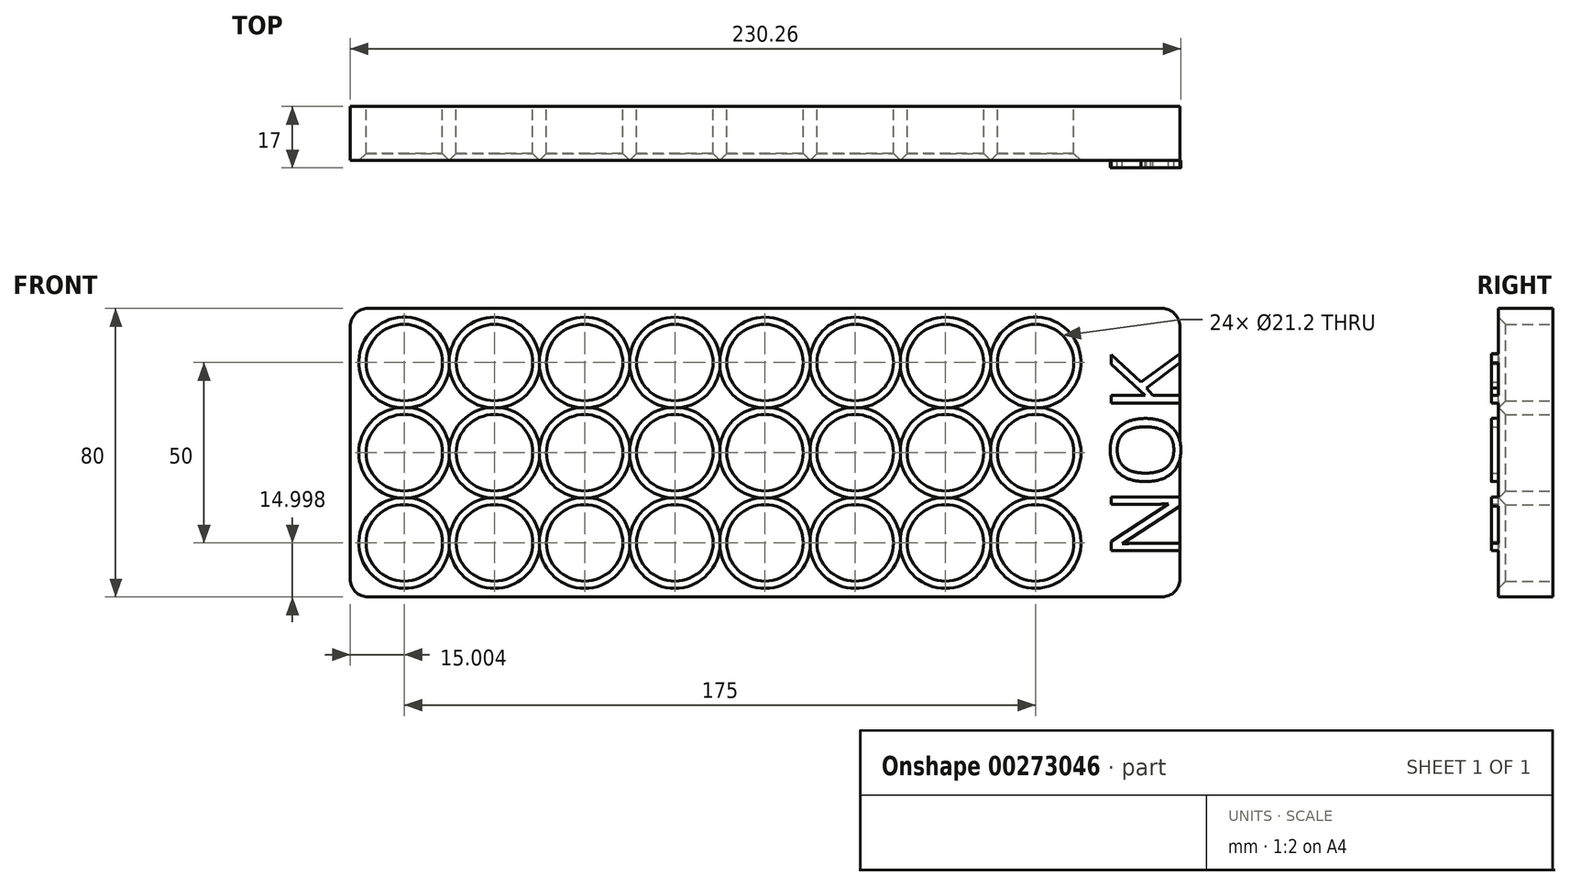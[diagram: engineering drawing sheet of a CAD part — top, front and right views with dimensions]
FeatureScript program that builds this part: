
annotation { "Feature Type Name" : "Feature", "Feature Type Description" : "" }
export const myFeature = defineFeature(function(context is Context, id is Id, definition is map)
    precondition{}
    {
        {
            var Q0;
            Q0=qCreatedBy(makeId("Front.planeOp"),FACE);
            var sketch = newSketch(context, id + "F0", { "sketchPlane" : qUnion([Q0])});
            skLineSegment(sketch, "E0.bottom", {"start": v(-104.74, 155.68) * mm, "end": v(125.26, 155.68) * mm});
            skLineSegment(sketch, "E0.top", {"start": v(-104.74, 75.68) * mm, "end": v(125.26, 75.68) * mm});
            skLineSegment(sketch, "E0.left", {"start": v(-104.74, 155.68) * mm, "end": v(-104.74, 75.68) * mm});
            skLineSegment(sketch, "E0.right", {"start": v(125.26, 155.68) * mm, "end": v(125.26, 75.68) * mm});
            skCircle(sketch, "E1", {"center": v(-89.74, 140.68) * mm, "radius": 10.6 * mm});
            skCircle(sketch, "E2.0.1.0", {"center": v(-89.74, 115.68) * mm, "radius": 10.6 * mm});
            skCircle(sketch, "E2.0.2.0", {"center": v(-89.74, 90.68) * mm, "radius": 10.6 * mm});
            skCircle(sketch, "E2.1.0.0", {"center": v(-64.74, 140.68) * mm, "radius": 10.6 * mm});
            skCircle(sketch, "E2.1.1.0", {"center": v(-64.74, 115.68) * mm, "radius": 10.6 * mm});
            skCircle(sketch, "E2.1.2.0", {"center": v(-64.74, 90.68) * mm, "radius": 10.6 * mm});
            skCircle(sketch, "E2.2.0.0", {"center": v(-39.74, 140.68) * mm, "radius": 10.6 * mm});
            skCircle(sketch, "E2.2.1.0", {"center": v(-39.74, 115.68) * mm, "radius": 10.6 * mm});
            skCircle(sketch, "E2.2.2.0", {"center": v(-39.74, 90.68) * mm, "radius": 10.6 * mm});
            skCircle(sketch, "E2.3.0.0", {"center": v(-14.74, 140.68) * mm, "radius": 10.6 * mm});
            skCircle(sketch, "E2.3.1.0", {"center": v(-14.74, 115.68) * mm, "radius": 10.6 * mm});
            skCircle(sketch, "E2.3.2.0", {"center": v(-14.74, 90.68) * mm, "radius": 10.6 * mm});
            skCircle(sketch, "E2.4.0.0", {"center": v(10.26, 140.68) * mm, "radius": 10.6 * mm});
            skCircle(sketch, "E2.4.1.0", {"center": v(10.26, 115.68) * mm, "radius": 10.6 * mm});
            skCircle(sketch, "E2.4.2.0", {"center": v(10.26, 90.68) * mm, "radius": 10.6 * mm});
            skCircle(sketch, "E2.5.0.0", {"center": v(35.26, 140.68) * mm, "radius": 10.6 * mm});
            skCircle(sketch, "E2.5.1.0", {"center": v(35.26, 115.68) * mm, "radius": 10.6 * mm});
            skCircle(sketch, "E2.5.2.0", {"center": v(35.26, 90.68) * mm, "radius": 10.6 * mm});
            skCircle(sketch, "E2.6.0.0", {"center": v(60.26, 140.68) * mm, "radius": 10.6 * mm});
            skCircle(sketch, "E2.6.1.0", {"center": v(60.26, 115.68) * mm, "radius": 10.6 * mm});
            skCircle(sketch, "E2.6.2.0", {"center": v(60.26, 90.68) * mm, "radius": 10.6 * mm});
            skCircle(sketch, "E2.7.0.0", {"center": v(85.26, 140.68) * mm, "radius": 10.6 * mm});
            skCircle(sketch, "E2.7.1.0", {"center": v(85.26, 115.68) * mm, "radius": 10.6 * mm});
            skCircle(sketch, "E2.7.2.0", {"center": v(85.26, 90.68) * mm, "radius": 10.6 * mm});
            skLineSegment(sketch, "E2.direction1", {"start": v(-89.74, 140.68) * mm, "end": v(-64.74, 140.68) * mm, "construction": true});
            skLineSegment(sketch, "E2.direction2", {"start": v(-89.74, 140.68) * mm, "end": v(-89.74, 115.68) * mm, "construction": true});
            skSolve(sketch);
        }
        {
            var Q0;
            Q0=qSketchRegion(id+"F0",true);
            extrude(context, id + "F1", {"entities" : qUnion([Q0]), "depth" : 15 * mm});
        }
        {
            var Q0;
            Q0=makeQuery(id+"FWD52A0zWoIziQt_1.boolean.opBoolean","MERGE",EDGE,{"derivedFrom":[makeQuery(id+"F1.opExtrude","SWEPT_EDGE",EDGE,{"disambiguationData":[OSD([sQuery(id+"F0.wireOp",EDGE,"E0.bottom"),sQuery(id+"F0.wireOp",EDGE,"E0.right")])]}),makeQuery(id+"FWD52A0zWoIziQt_1.opExtrude","SWEPT_EDGE",EDGE,{"disambiguationData":[OSD([sQuery(id+"FsMENEcZQ2nr4Gj_1.wireOp",EDGE,"yo0ZsG5o-0MR3-nl2M-1CvW-6fkTD8x1XfXn.bottom"),sQuery(id+"FsMENEcZQ2nr4Gj_1.wireOp",EDGE,"yo0ZsG5o-0MR3-nl2M-1CvW-6fkTD8x1XfXn.left")])]})]});
            var Q1;
            Q1=makeQuery(id+"FWD52A0zWoIziQt_1.boolean.opBoolean","MERGE",EDGE,{"derivedFrom":[makeQuery(id+"F1.opExtrude","SWEPT_EDGE",EDGE,{"disambiguationData":[OSD([sQuery(id+"F0.wireOp",EDGE,"E0.top"),sQuery(id+"F0.wireOp",EDGE,"E0.right")])]}),makeQuery(id+"FWD52A0zWoIziQt_1.opExtrude","SWEPT_EDGE",EDGE,{"disambiguationData":[OSD([sQuery(id+"FsMENEcZQ2nr4Gj_1.wireOp",EDGE,"yo0ZsG5o-0MR3-nl2M-1CvW-6fkTD8x1XfXn.top"),sQuery(id+"FsMENEcZQ2nr4Gj_1.wireOp",EDGE,"yo0ZsG5o-0MR3-nl2M-1CvW-6fkTD8x1XfXn.left")])]})]});
            var Q2;
            Q2=makeQuery(id+"FWD52A0zWoIziQt_1.boolean.opBoolean","MERGE",EDGE,{"derivedFrom":[makeQuery(id+"F1.opExtrude","SWEPT_EDGE",EDGE,{"disambiguationData":[OSD([sQuery(id+"F0.wireOp",EDGE,"E0.bottom"),sQuery(id+"F0.wireOp",EDGE,"E0.left")])]}),makeQuery(id+"FWD52A0zWoIziQt_1.opExtrude","SWEPT_EDGE",EDGE,{"disambiguationData":[OSD([sQuery(id+"FsMENEcZQ2nr4Gj_1.wireOp",EDGE,"yo0ZsG5o-0MR3-nl2M-1CvW-6fkTD8x1XfXn.bottom"),sQuery(id+"FsMENEcZQ2nr4Gj_1.wireOp",EDGE,"yo0ZsG5o-0MR3-nl2M-1CvW-6fkTD8x1XfXn.right")])]})]});
            var Q3;
            Q3=makeQuery(id+"FWD52A0zWoIziQt_1.boolean.opBoolean","MERGE",EDGE,{"derivedFrom":[makeQuery(id+"F1.opExtrude","SWEPT_EDGE",EDGE,{"disambiguationData":[OSD([sQuery(id+"F0.wireOp",EDGE,"E0.top"),sQuery(id+"F0.wireOp",EDGE,"E0.left")])]}),makeQuery(id+"FWD52A0zWoIziQt_1.opExtrude","SWEPT_EDGE",EDGE,{"disambiguationData":[OSD([sQuery(id+"FsMENEcZQ2nr4Gj_1.wireOp",EDGE,"yo0ZsG5o-0MR3-nl2M-1CvW-6fkTD8x1XfXn.top"),sQuery(id+"FsMENEcZQ2nr4Gj_1.wireOp",EDGE,"yo0ZsG5o-0MR3-nl2M-1CvW-6fkTD8x1XfXn.right")])]})]});
            fillet(context, id + "F2", {"entities" : qUnion([Q0, Q1, Q2, Q3]), "radius" : 5 * mm, "tangentPropagation" : true, "allowEdgeOverflow" : false});
        }
        {
            var Q0;
            Q0=makeQuery(id+"F1.opExtrude","CAP_EDGE",EDGE,{"disambiguationData":[OSD([sQuery(id+"F0.wireOp",EDGE,"E2.0.5.0")])],"isStart":false});
            var Q1;
            Q1=makeQuery(id+"F1.opExtrude","CAP_EDGE",EDGE,{"disambiguationData":[OSD([sQuery(id+"F0.wireOp",EDGE,"E2.0.6.0")])],"isStart":false});
            var Q2;
            Q2=makeQuery(id+"F1.opExtrude","CAP_EDGE",EDGE,{"disambiguationData":[OSD([sQuery(id+"F0.wireOp",EDGE,"E2.0.7.0")])],"isStart":false});
            var Q3;
            Q3=makeQuery(id+"F1.opExtrude","CAP_EDGE",EDGE,{"disambiguationData":[OSD([sQuery(id+"F0.wireOp",EDGE,"E2.1.7.0")])],"isStart":false});
            var Q4;
            Q4=makeQuery(id+"F1.opExtrude","CAP_EDGE",EDGE,{"disambiguationData":[OSD([sQuery(id+"F0.wireOp",EDGE,"E2.1.6.0")])],"isStart":false});
            var Q5;
            Q5=makeQuery(id+"F1.opExtrude","CAP_EDGE",EDGE,{"disambiguationData":[OSD([sQuery(id+"F0.wireOp",EDGE,"E2.1.5.0")])],"isStart":false});
            var Q6;
            Q6=makeQuery(id+"F1.opExtrude","CAP_EDGE",EDGE,{"disambiguationData":[OSD([sQuery(id+"F0.wireOp",EDGE,"E2.0.4.0")])],"isStart":false});
            var Q7;
            Q7=makeQuery(id+"F1.opExtrude","CAP_EDGE",EDGE,{"disambiguationData":[OSD([sQuery(id+"F0.wireOp",EDGE,"E2.0.3.0")])],"isStart":false});
            var Q8;
            Q8=makeQuery(id+"F1.opExtrude","CAP_EDGE",EDGE,{"disambiguationData":[OSD([sQuery(id+"F0.wireOp",EDGE,"E2.0.2.0")])],"isStart":false});
            var Q9;
            Q9=makeQuery(id+"F1.opExtrude","CAP_EDGE",EDGE,{"disambiguationData":[OSD([sQuery(id+"F0.wireOp",EDGE,"E2.0.1.0")])],"isStart":false});
            var Q10;
            Q10=makeQuery(id+"F1.opExtrude","CAP_EDGE",EDGE,{"disambiguationData":[OSD([sQuery(id+"F0.wireOp",EDGE,"E1")])],"isStart":false});
            var Q11;
            Q11=makeQuery(id+"F1.opExtrude","CAP_EDGE",EDGE,{"disambiguationData":[OSD([sQuery(id+"F0.wireOp",EDGE,"E2.1.0.0")])],"isStart":false});
            var Q12;
            Q12=makeQuery(id+"F1.opExtrude","CAP_EDGE",EDGE,{"disambiguationData":[OSD([sQuery(id+"F0.wireOp",EDGE,"E2.1.1.0")])],"isStart":false});
            var Q13;
            Q13=makeQuery(id+"F1.opExtrude","CAP_EDGE",EDGE,{"disambiguationData":[OSD([sQuery(id+"F0.wireOp",EDGE,"E2.1.2.0")])],"isStart":false});
            var Q14;
            Q14=makeQuery(id+"F1.opExtrude","CAP_EDGE",EDGE,{"disambiguationData":[OSD([sQuery(id+"F0.wireOp",EDGE,"E2.1.3.0")])],"isStart":false});
            var Q15;
            Q15=makeQuery(id+"F1.opExtrude","CAP_EDGE",EDGE,{"disambiguationData":[OSD([sQuery(id+"F0.wireOp",EDGE,"E2.1.4.0")])],"isStart":false});
            var Q16;
            Q16=makeQuery(id+"F1.opExtrude","CAP_EDGE",EDGE,{"disambiguationData":[OSD([sQuery(id+"F0.wireOp",EDGE,"E2.2.7.0")])],"isStart":false});
            var Q17;
            Q17=makeQuery(id+"F1.opExtrude","CAP_EDGE",EDGE,{"disambiguationData":[OSD([sQuery(id+"F0.wireOp",EDGE,"E2.2.6.0")])],"isStart":false});
            var Q18;
            Q18=makeQuery(id+"F1.opExtrude","CAP_EDGE",EDGE,{"disambiguationData":[OSD([sQuery(id+"F0.wireOp",EDGE,"E2.2.5.0")])],"isStart":false});
            var Q19;
            Q19=makeQuery(id+"F1.opExtrude","CAP_EDGE",EDGE,{"disambiguationData":[OSD([sQuery(id+"F0.wireOp",EDGE,"E2.2.4.0")])],"isStart":false});
            var Q20;
            Q20=makeQuery(id+"F1.opExtrude","CAP_EDGE",EDGE,{"disambiguationData":[OSD([sQuery(id+"F0.wireOp",EDGE,"E2.2.3.0")])],"isStart":false});
            var Q21;
            Q21=makeQuery(id+"F1.opExtrude","CAP_EDGE",EDGE,{"disambiguationData":[OSD([sQuery(id+"F0.wireOp",EDGE,"E2.2.2.0")])],"isStart":false});
            var Q22;
            Q22=makeQuery(id+"F1.opExtrude","CAP_EDGE",EDGE,{"disambiguationData":[OSD([sQuery(id+"F0.wireOp",EDGE,"E2.2.1.0")])],"isStart":false});
            var Q23;
            Q23=makeQuery(id+"F1.opExtrude","CAP_EDGE",EDGE,{"disambiguationData":[OSD([sQuery(id+"F0.wireOp",EDGE,"E2.2.0.0")])],"isStart":false});
            var Q24;
            Q24=makeQuery(id+"F1.opExtrude","CAP_EDGE",EDGE,{"disambiguationData":[OSD([sQuery(id+"F0.wireOp",EDGE,"E2.3.0.0")])],"isStart":false});
            var Q25;
            Q25=makeQuery(id+"F1.opExtrude","CAP_EDGE",EDGE,{"disambiguationData":[OSD([sQuery(id+"F0.wireOp",EDGE,"E2.3.1.0")])],"isStart":false});
            var Q26;
            Q26=makeQuery(id+"F1.opExtrude","CAP_EDGE",EDGE,{"disambiguationData":[OSD([sQuery(id+"F0.wireOp",EDGE,"E2.3.2.0")])],"isStart":false});
            var Q27;
            Q27=makeQuery(id+"F1.opExtrude","CAP_EDGE",EDGE,{"disambiguationData":[OSD([sQuery(id+"F0.wireOp",EDGE,"E2.3.3.0")])],"isStart":false});
            var Q28;
            Q28=makeQuery(id+"F1.opExtrude","CAP_EDGE",EDGE,{"disambiguationData":[OSD([sQuery(id+"F0.wireOp",EDGE,"E2.3.4.0")])],"isStart":false});
            var Q29;
            Q29=makeQuery(id+"F1.opExtrude","CAP_EDGE",EDGE,{"disambiguationData":[OSD([sQuery(id+"F0.wireOp",EDGE,"E2.3.5.0")])],"isStart":false});
            var Q30;
            Q30=makeQuery(id+"F1.opExtrude","CAP_EDGE",EDGE,{"disambiguationData":[OSD([sQuery(id+"F0.wireOp",EDGE,"E2.3.6.0")])],"isStart":false});
            var Q31;
            Q31=makeQuery(id+"F1.opExtrude","CAP_EDGE",EDGE,{"disambiguationData":[OSD([sQuery(id+"F0.wireOp",EDGE,"E2.3.7.0")])],"isStart":false});
            var Q32;
            Q32=makeQuery(id+"F1.opExtrude","CAP_EDGE",EDGE,{"disambiguationData":[OSD([sQuery(id+"F0.wireOp",EDGE,"E2.4.7.0")])],"isStart":false});
            var Q33;
            Q33=makeQuery(id+"F1.opExtrude","CAP_EDGE",EDGE,{"disambiguationData":[OSD([sQuery(id+"F0.wireOp",EDGE,"E2.4.6.0")])],"isStart":false});
            var Q34;
            Q34=makeQuery(id+"F1.opExtrude","CAP_EDGE",EDGE,{"disambiguationData":[OSD([sQuery(id+"F0.wireOp",EDGE,"E2.4.5.0")])],"isStart":false});
            var Q35;
            Q35=makeQuery(id+"F1.opExtrude","CAP_EDGE",EDGE,{"disambiguationData":[OSD([sQuery(id+"F0.wireOp",EDGE,"E2.4.4.0")])],"isStart":false});
            var Q36;
            Q36=makeQuery(id+"F1.opExtrude","CAP_EDGE",EDGE,{"disambiguationData":[OSD([sQuery(id+"F0.wireOp",EDGE,"E2.4.3.0")])],"isStart":false});
            var Q37;
            Q37=makeQuery(id+"F1.opExtrude","CAP_EDGE",EDGE,{"disambiguationData":[OSD([sQuery(id+"F0.wireOp",EDGE,"E2.4.2.0")])],"isStart":false});
            var Q38;
            Q38=makeQuery(id+"F1.opExtrude","CAP_EDGE",EDGE,{"disambiguationData":[OSD([sQuery(id+"F0.wireOp",EDGE,"E2.4.1.0")])],"isStart":false});
            var Q39;
            Q39=makeQuery(id+"F1.opExtrude","CAP_EDGE",EDGE,{"disambiguationData":[OSD([sQuery(id+"F0.wireOp",EDGE,"E2.4.0.0")])],"isStart":false});
            var Q40;
            Q40=makeQuery(id+"F1.opExtrude","CAP_EDGE",EDGE,{"disambiguationData":[OSD([sQuery(id+"F0.wireOp",EDGE,"E2.5.0.0")])],"isStart":false});
            var Q41;
            Q41=makeQuery(id+"F1.opExtrude","CAP_EDGE",EDGE,{"disambiguationData":[OSD([sQuery(id+"F0.wireOp",EDGE,"E2.5.1.0")])],"isStart":false});
            var Q42;
            Q42=makeQuery(id+"F1.opExtrude","CAP_EDGE",EDGE,{"disambiguationData":[OSD([sQuery(id+"F0.wireOp",EDGE,"E2.6.0.0")])],"isStart":false});
            var Q43;
            Q43=makeQuery(id+"F1.opExtrude","CAP_EDGE",EDGE,{"disambiguationData":[OSD([sQuery(id+"F0.wireOp",EDGE,"E2.6.1.0")])],"isStart":false});
            var Q44;
            Q44=makeQuery(id+"F1.opExtrude","CAP_EDGE",EDGE,{"disambiguationData":[OSD([sQuery(id+"F0.wireOp",EDGE,"E2.7.0.0")])],"isStart":false});
            var Q45;
            Q45=makeQuery(id+"F1.opExtrude","CAP_EDGE",EDGE,{"disambiguationData":[OSD([sQuery(id+"F0.wireOp",EDGE,"E2.7.1.0")])],"isStart":false});
            var Q46;
            Q46=makeQuery(id+"F1.opExtrude","CAP_EDGE",EDGE,{"disambiguationData":[OSD([sQuery(id+"F0.wireOp",EDGE,"E2.5.2.0")])],"isStart":false});
            var Q47;
            Q47=makeQuery(id+"F1.opExtrude","CAP_EDGE",EDGE,{"disambiguationData":[OSD([sQuery(id+"F0.wireOp",EDGE,"E2.6.2.0")])],"isStart":false});
            var Q48;
            Q48=makeQuery(id+"F1.opExtrude","CAP_EDGE",EDGE,{"disambiguationData":[OSD([sQuery(id+"F0.wireOp",EDGE,"E2.5.3.0")])],"isStart":false});
            var Q49;
            Q49=makeQuery(id+"F1.opExtrude","CAP_EDGE",EDGE,{"disambiguationData":[OSD([sQuery(id+"F0.wireOp",EDGE,"E2.6.3.0")])],"isStart":false});
            var Q50;
            Q50=makeQuery(id+"F1.opExtrude","CAP_EDGE",EDGE,{"disambiguationData":[OSD([sQuery(id+"F0.wireOp",EDGE,"E2.7.2.0")])],"isStart":false});
            var Q51;
            Q51=makeQuery(id+"F1.opExtrude","CAP_EDGE",EDGE,{"disambiguationData":[OSD([sQuery(id+"F0.wireOp",EDGE,"E2.7.3.0")])],"isStart":false});
            var Q52;
            Q52=makeQuery(id+"F1.opExtrude","CAP_EDGE",EDGE,{"disambiguationData":[OSD([sQuery(id+"F0.wireOp",EDGE,"E2.5.4.0")])],"isStart":false});
            var Q53;
            Q53=makeQuery(id+"F1.opExtrude","CAP_EDGE",EDGE,{"disambiguationData":[OSD([sQuery(id+"F0.wireOp",EDGE,"E2.6.4.0")])],"isStart":false});
            var Q54;
            Q54=makeQuery(id+"F1.opExtrude","CAP_EDGE",EDGE,{"disambiguationData":[OSD([sQuery(id+"F0.wireOp",EDGE,"E2.5.5.0")])],"isStart":false});
            var Q55;
            Q55=makeQuery(id+"F1.opExtrude","CAP_EDGE",EDGE,{"disambiguationData":[OSD([sQuery(id+"F0.wireOp",EDGE,"E2.6.5.0")])],"isStart":false});
            var Q56;
            Q56=makeQuery(id+"F1.opExtrude","CAP_EDGE",EDGE,{"disambiguationData":[OSD([sQuery(id+"F0.wireOp",EDGE,"E2.7.4.0")])],"isStart":false});
            var Q57;
            Q57=makeQuery(id+"F1.opExtrude","CAP_EDGE",EDGE,{"disambiguationData":[OSD([sQuery(id+"F0.wireOp",EDGE,"E2.7.5.0")])],"isStart":false});
            var Q58;
            Q58=makeQuery(id+"F1.opExtrude","CAP_EDGE",EDGE,{"disambiguationData":[OSD([sQuery(id+"F0.wireOp",EDGE,"E2.7.6.0")])],"isStart":false});
            var Q59;
            Q59=makeQuery(id+"F1.opExtrude","CAP_EDGE",EDGE,{"disambiguationData":[OSD([sQuery(id+"F0.wireOp",EDGE,"E2.6.6.0")])],"isStart":false});
            var Q60;
            Q60=makeQuery(id+"F1.opExtrude","CAP_EDGE",EDGE,{"disambiguationData":[OSD([sQuery(id+"F0.wireOp",EDGE,"E2.5.6.0")])],"isStart":false});
            var Q61;
            Q61=makeQuery(id+"F1.opExtrude","CAP_EDGE",EDGE,{"disambiguationData":[OSD([sQuery(id+"F0.wireOp",EDGE,"E2.5.7.0")])],"isStart":false});
            var Q62;
            Q62=makeQuery(id+"F1.opExtrude","CAP_EDGE",EDGE,{"disambiguationData":[OSD([sQuery(id+"F0.wireOp",EDGE,"E2.6.7.0")])],"isStart":false});
            var Q63;
            Q63=makeQuery(id+"F1.opExtrude","CAP_EDGE",EDGE,{"disambiguationData":[OSD([sQuery(id+"F0.wireOp",EDGE,"E2.7.7.0")])],"isStart":false});
            chamfer(context, id + "F3", {"entities" : qUnion([Q0, Q1, Q2, Q3, Q4, Q5, Q6, Q7, Q8, Q9, Q10, Q11, Q12, Q13, Q14, Q15, Q16, Q17, Q18, Q19, Q20, Q21, Q22, Q23, Q24, Q25, Q26, Q27, Q28, Q29, Q30, Q31, Q32, Q33, Q34, Q35, Q36, Q37, Q38, Q39, Q40, Q41, Q42, Q43, Q44, Q45, Q46, Q47, Q48, Q49, Q50, Q51, Q52, Q53, Q54, Q55, Q56, Q57, Q58, Q59, Q60, Q61, Q62, Q63]), "width" : 2 * mm, "tangentPropagation" : true});
        }
        {
            var Q0;
            Q0=makeQuery(id+"F3.opChamfer","SPLIT",FACE,{"disambiguationData":[OD(14.0)],"derivedFrom":makeQuery(id+"F1.opExtrude","CAP_FACE",FACE,{"disambiguationData":[OSD([sQuery(id+"F0.wireOp",EDGE,"E0.bottom"),sQuery(id+"F0.wireOp",EDGE,"E0.top"),sQuery(id+"F0.wireOp",EDGE,"E0.left"),sQuery(id+"F0.wireOp",EDGE,"E0.right"),sQuery(id+"F0.wireOp",EDGE,"E1"),sQuery(id+"F0.wireOp",EDGE,"E2.0.1.0"),sQuery(id+"F0.wireOp",EDGE,"E2.0.2.0"),sQuery(id+"F0.wireOp",EDGE,"E2.1.0.0"),sQuery(id+"F0.wireOp",EDGE,"E2.1.1.0"),sQuery(id+"F0.wireOp",EDGE,"E2.1.2.0"),sQuery(id+"F0.wireOp",EDGE,"E2.2.0.0"),sQuery(id+"F0.wireOp",EDGE,"E2.2.1.0"),sQuery(id+"F0.wireOp",EDGE,"E2.2.2.0"),sQuery(id+"F0.wireOp",EDGE,"E2.3.0.0"),sQuery(id+"F0.wireOp",EDGE,"E2.3.1.0"),sQuery(id+"F0.wireOp",EDGE,"E2.3.2.0"),sQuery(id+"F0.wireOp",EDGE,"E2.4.0.0"),sQuery(id+"F0.wireOp",EDGE,"E2.4.1.0"),sQuery(id+"F0.wireOp",EDGE,"E2.4.2.0"),sQuery(id+"F0.wireOp",EDGE,"E2.5.0.0"),sQuery(id+"F0.wireOp",EDGE,"E2.5.1.0"),sQuery(id+"F0.wireOp",EDGE,"E2.5.2.0"),sQuery(id+"F0.wireOp",EDGE,"E2.6.0.0"),sQuery(id+"F0.wireOp",EDGE,"E2.6.1.0"),sQuery(id+"F0.wireOp",EDGE,"E2.6.2.0"),sQuery(id+"F0.wireOp",EDGE,"E2.7.0.0"),sQuery(id+"F0.wireOp",EDGE,"E2.7.1.0"),sQuery(id+"F0.wireOp",EDGE,"E2.7.2.0")])],"isStart":false})});
            var sketch = newSketch(context, id + "F4", { "sketchPlane" : qUnion([Q0])});
            skText(sketch, "E3", { "text": "NOK", "fontName": "OpenSans-Regular.ttf"});
            const initialGuessF4  = {"E3": [0.12526, 0.08594, 0, 1, 0.0192]};
            skSetInitialGuess(sketch, initialGuessF4);
            skSolve(sketch);
        }
        {
            var Q0;
            Q0=qSketchRegion(id+"F4",true);
            extrude(context, id + "F5", {"entities" : qUnion([Q0]), "operationType" : NewBodyOperationType.ADD, "depth" : 2 * mm});
        }
    });
